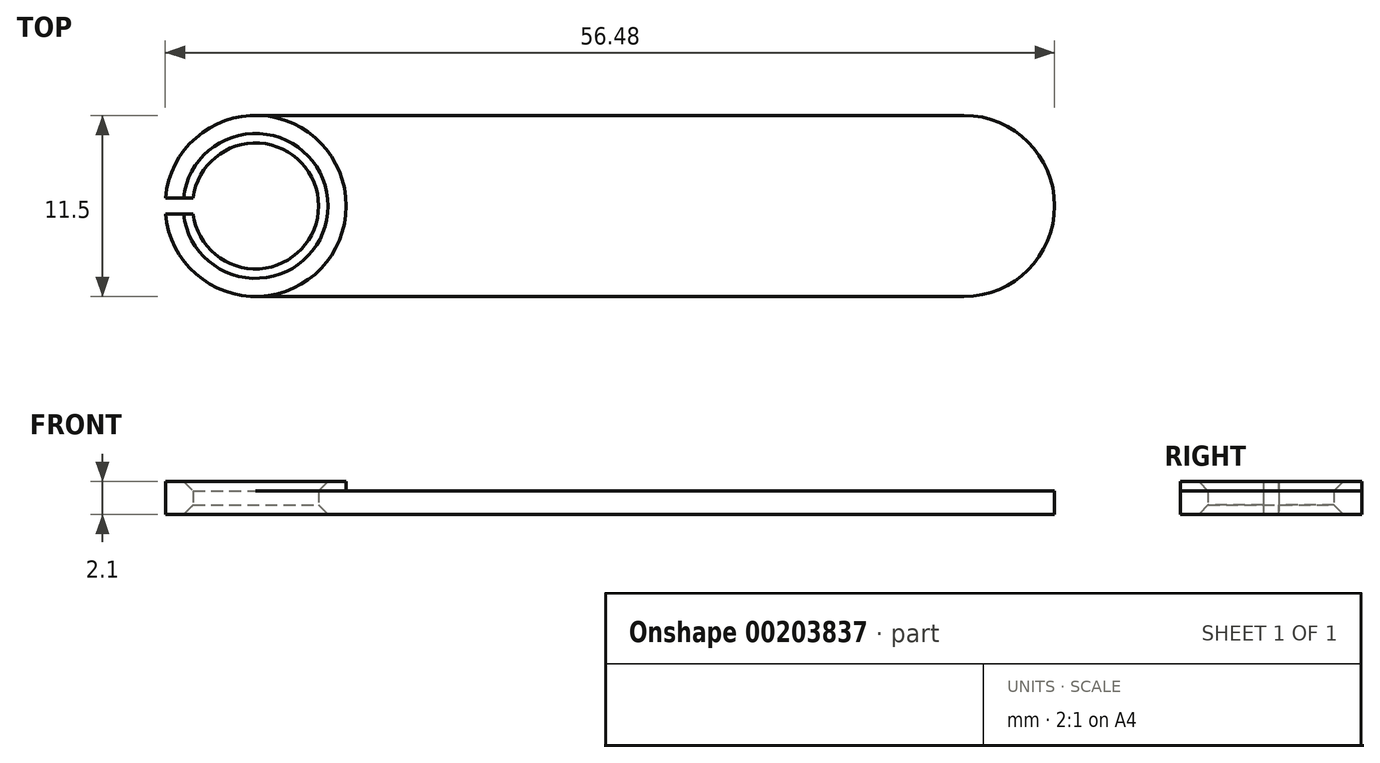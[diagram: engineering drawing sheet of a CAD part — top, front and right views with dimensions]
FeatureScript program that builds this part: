
annotation { "Feature Type Name" : "Feature", "Feature Type Description" : "" }
export const myFeature = defineFeature(function(context is Context, id is Id, definition is map)
    precondition{}
    {
        {
            var Q0;
            Q0=qCreatedBy(makeId("Top.planeOp"),FACE);
            var sketch = newSketch(context, id + "F0", { "sketchPlane" : qUnion([Q0])});
            skCircle(sketch, "E0", {"center": v(0, 0) * mm, "radius": 4 * mm});
            skArc(sketch, "E1", {"start": v(0, 5.75) * mm, "mid": v(-5.75, 0) * mm, "end": v(0, -5.75) * mm});
            skLineSegment(sketch, "E2", {"start": v(0, 5.75) * mm, "end": v(45, 5.75) * mm});
            skLineSegment(sketch, "E3", {"start": v(0, -5.75) * mm, "end": v(45, -5.75) * mm});
            skArc(sketch, "E4", {"start": v(45, -5.75) * mm, "mid": v(50.75, 0) * mm, "end": v(45, 5.75) * mm});
            skSolve(sketch);
        }
        {
            var Q0;
            Q0=qSketchRegion(id+"F0",true);
            extrude(context, id + "F1", {"entities" : qUnion([Q0]), "depth" : 1.5 * mm});
        }
        {
            var Q0;
            Q0=makeQuery(id+"F1.opExtrude","CAP_FACE",FACE,{"disambiguationData":[OSD([sQuery(id+"F0.wireOp",EDGE,"E0"),sQuery(id+"F0.wireOp",EDGE,"E1"),sQuery(id+"F0.wireOp",EDGE,"E2"),sQuery(id+"F0.wireOp",EDGE,"E3"),sQuery(id+"F0.wireOp",EDGE,"E4")])],"isStart":false});
            var sketch = newSketch(context, id + "F2", { "sketchPlane" : qUnion([Q0])});
            skCircle(sketch, "E5", {"center": v(0, 0) * mm, "radius": 4 * mm});
            skCircle(sketch, "E6", {"center": v(0, 0) * mm, "radius": 5.75 * mm});
            skSolve(sketch);
        }
        {
            var Q0;
            Q0=qSketchRegion(id+"F2",true);
            extrude(context, id + "F3", {"entities" : qUnion([Q0]), "operationType" : NewBodyOperationType.ADD, "depth" : 0.6 * mm});
        }
        {
            var Q0;
            Q0=makeQuery(id+"F1.opExtrude","CAP_FACE",FACE,{"disambiguationData":[OSD([sQuery(id+"F0.wireOp",EDGE,"E0"),sQuery(id+"F0.wireOp",EDGE,"E1"),sQuery(id+"F0.wireOp",EDGE,"E2"),sQuery(id+"F0.wireOp",EDGE,"E3"),sQuery(id+"F0.wireOp",EDGE,"E4")])],"isStart":true});
            var sketch = newSketch(context, id + "F4", { "sketchPlane" : qUnion([Q0])});
            skLineSegment(sketch, "E7", {"start": v(-3.97, 0) * mm, "end": v(-3.97, 0.5) * mm});
            skLineSegment(sketch, "E8", {"start": v(-3.97, 0.5) * mm, "end": v(-5.75, 0.5) * mm});
            skLineSegment(sketch, "E9", {"start": v(-5.75, 0.5) * mm, "end": v(-5.75, 0) * mm});
            skLineSegment(sketch, "E10", {"start": v(-5.75, 0) * mm, "end": v(-5.75, -0.5) * mm});
            skLineSegment(sketch, "E11", {"start": v(-5.75, -0.5) * mm, "end": v(-3.97, -0.5) * mm});
            skLineSegment(sketch, "E12", {"start": v(-3.97, -0.5) * mm, "end": v(-3.97, 0) * mm});
            skSolve(sketch);
        }
        {
            var Q0;
            Q0=qSketchRegion(id+"F4",true);
            var Q1;
            Q1=makeQuery(id+"F3.opExtrude","CAP_FACE",FACE,{"disambiguationData":[OSD([sQuery(id+"F2.wireOp",EDGE,"E5"),sQuery(id+"F2.wireOp",EDGE,"E6")])],"isStart":false});
            extrude(context, id + "F5", {"entities" : qUnion([Q0]), "operationType" : NewBodyOperationType.REMOVE, "endBound" : BoundingType.UP_TO_SURFACE, "oppositeDirection" : true, "endBoundEntityFace" : qUnion([Q1]), "depth" : 25 * mm});
        }
        {
            var Q0;
            Q0=makeQuery(id+"F3.opExtrude","CAP_EDGE",EDGE,{"disambiguationData":[OSD([sQuery(id+"F2.wireOp",EDGE,"E6")])],"isStart":true});
            var Q1;
            Q1=makeQuery(id+"F3.opExtrude","CAP_EDGE",EDGE,{"disambiguationData":[OSD([sQuery(id+"F2.wireOp",EDGE,"E5")])],"isStart":false});
            var Q2;
            Q2=makeQuery(id+"F1.opExtrude","CAP_EDGE",EDGE,{"disambiguationData":[OSD([sQuery(id+"F0.wireOp",EDGE,"E0")])],"isStart":true});
            chamfer(context, id + "F6", {"entities" : qUnion([Q0, Q1, Q2]), "width" : 0.6 * mm, "tangentPropagation" : true});
        }
    });
